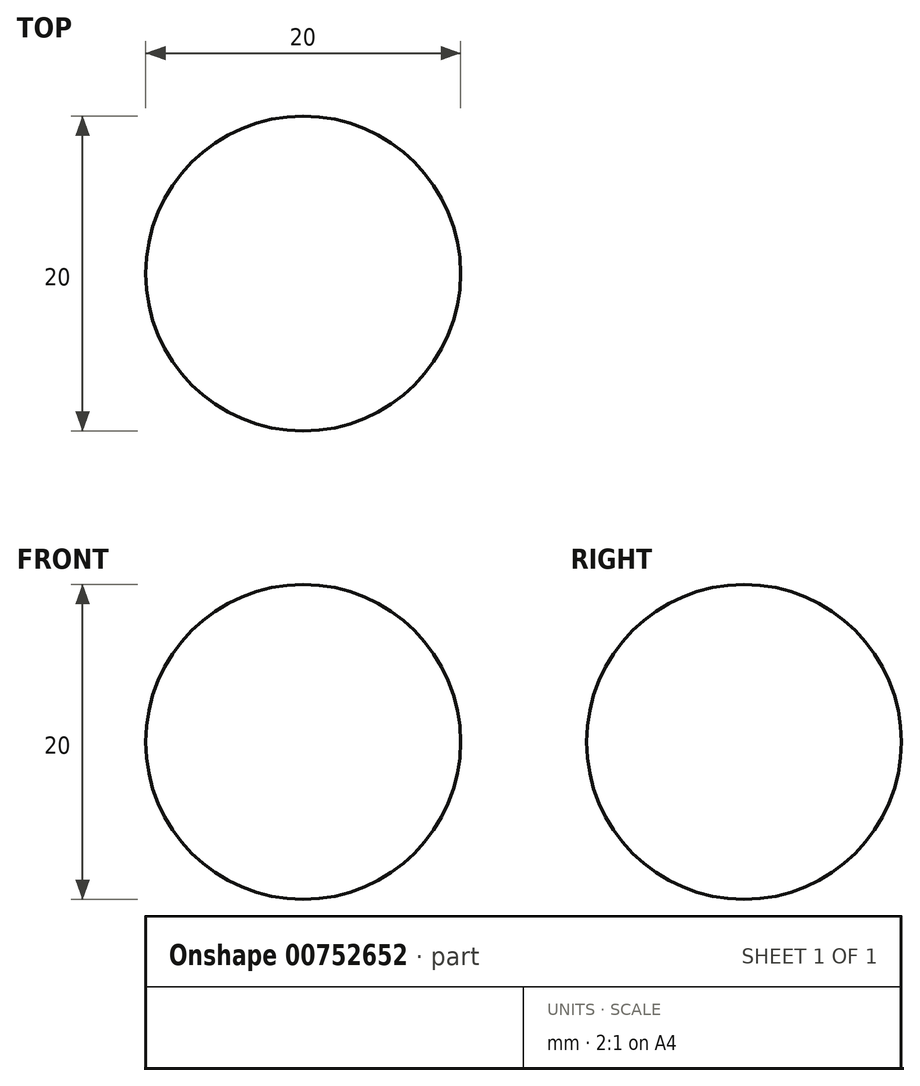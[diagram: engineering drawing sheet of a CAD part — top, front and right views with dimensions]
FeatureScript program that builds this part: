
annotation { "Feature Type Name" : "Feature", "Feature Type Description" : "" }
export const myFeature = defineFeature(function(context is Context, id is Id, definition is map)
    precondition{}
    {
        {
            var Q0;
            Q0=qCreatedBy(makeId("Front.planeOp"),FACE);
            var sketch = newSketch(context, id + "F0", { "sketchPlane" : qUnion([Q0])});
            skArc(sketch, "E0", {"start": v(0, -10) * mm, "mid": v(10, 0) * mm, "end": v(0, 10) * mm});
            skLineSegment(sketch, "E1", {"start": v(0, -10) * mm, "end": v(0, 10) * mm});
            skSolve(sketch);
        }
        {
            var Q0;
            Q0=qCreatedBy(makeId("Top.planeOp"),FACE);
            var sketch = newSketch(context, id + "F1", { "sketchPlane" : qUnion([Q0])});
            skCircle(sketch, "E2", {"center": v(0, 0) * mm, "radius": 10 * mm, "construction": true});
            skSolve(sketch);
        }
        {
            var Q0;
            Q0=makeQuery(id+"F0.imprint","IMPRINT",FACE,{"disambiguationData":[TD([[makeQuery(id+"F0.imprint","IMPRINT",EDGE,{"derivedFrom":sQuery(id+"F0.wireOp",EDGE,"E0")}),1.0]])]});
            var Q1;
            Q1=sQuery(id+"F1.wireOp",EDGE,"E2");
            revolve(context, id + "F2", {"entities" : qUnion([Q0]), "axis" : qUnion([Q1]), "revolveType" : RevolveType.FULL});
        }
    });
